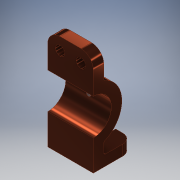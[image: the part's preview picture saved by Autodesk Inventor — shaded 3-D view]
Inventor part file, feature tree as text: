
AUTODESK INVENTOR PART (.ipt)
format: ipt  version: 2018 (Build 220112000, 112)  size: 176,640 bytes
history: native  units: mm
features: extrude x4, sketch x4, fillet x3, thread x1
ambient origin geometry x8: Origin, YZ Plane, XZ Plane, XY Plane, X Axis, Y Axis, Z Axis, Center Point
bodies: Solid1 (feature_tree)
feature tree (12):
  extrude  "Extrusion1"  Depth=51.0mm
  fillet  "Fillet1"  Radius=51.0mm
  fillet  "Fillet2"  Radius=11.0mm
  extrude  "Extrusion2"  Depth=48.0mm TaperAngle=0.0deg
  extrude  "Extrusion3"  Depth=10.0mm
  fillet  "Fillet3"  Radius=10.0mm
  extrude  "Extrusion4"  TaperAngle=0.0deg  [1 undecoded]
  thread  "Thread1"  [1 undecoded]
  sketch  "Sketch1"  dims[d0=41.0mm d1=107.0mm d2=51.0mm d3=11.0mm]
  sketch  "Sketch2"  dims[d4=30.0mm d5=48.0mm d6=0.0mm]
  sketch  "Sketch3"  dims[d7=13.0mm d8=2.0mm d9=10.0mm]
  sketch  "Sketch4"  dims[d10=10.0mm d11=0.0mm d12=0.0mm d14=13.0mm d15=6.5mm d16=16.0mm d17=6.5mm d18=11.0mm d19=0.0mm d20=10.0mm d21=5.0mm d22=11.0mm d23=0.0mm d24=10.0mm d25=0.0mm]
note: 2 required parameter values undecoded (feature->parameter linkage not recoverable at this tier; creation-order binding heuristic only, values carry confidence <= 0.55)
